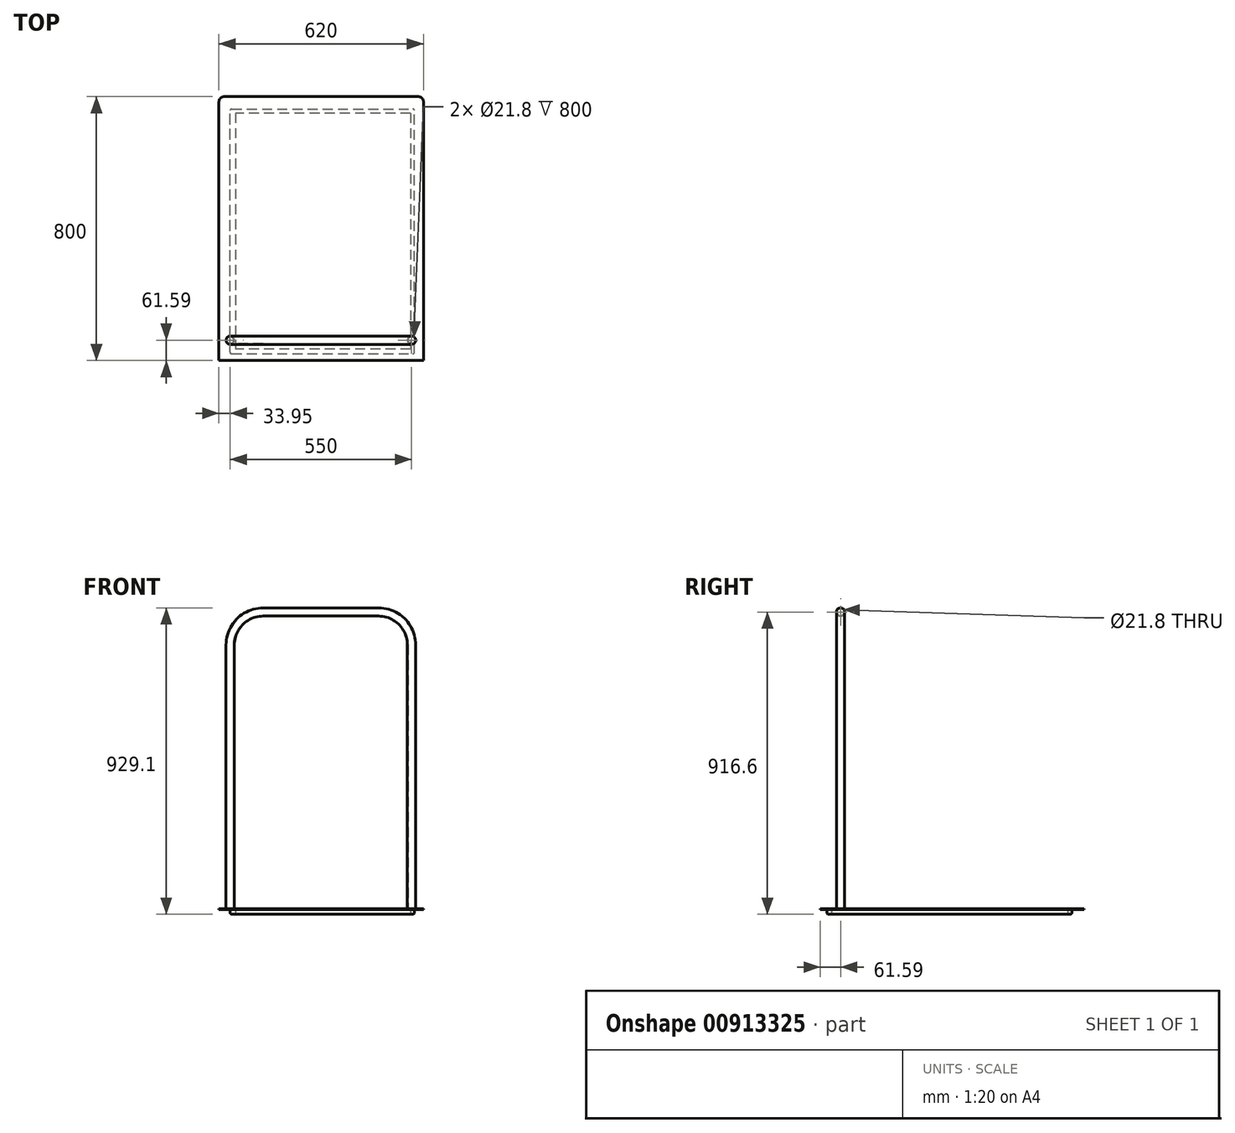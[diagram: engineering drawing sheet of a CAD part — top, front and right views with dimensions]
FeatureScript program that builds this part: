
annotation { "Feature Type Name" : "Feature", "Feature Type Description" : "" }
export const myFeature = defineFeature(function(context is Context, id is Id, definition is map)
    precondition{}
    {
        {
            var Q0;
            Q0=qCreatedBy(makeId("Top.planeOp"),FACE);
            var sketch = newSketch(context, id + "F0", { "sketchPlane" : qUnion([Q0])});
            skCircle(sketch, "E0", {"center": v(0, 0) * mm, "radius": 12.5 * mm});
            skCircle(sketch, "E1", {"center": v(0, 0) * mm, "radius": 10.9 * mm});
            skSolve(sketch);
        }
        {
            var Q0;
            Q0=qCreatedBy(makeId("Front.planeOp"),FACE);
            var sketch = newSketch(context, id + "F1", { "sketchPlane" : qUnion([Q0])});
            skLineSegment(sketch, "E2.top", {"start": v(100, 900) * mm, "end": v(450, 900) * mm});
            skLineSegment(sketch, "E2.left", {"start": v(0, 0) * mm, "end": v(0, 800) * mm});
            skLineSegment(sketch, "E2.right", {"start": v(550, 0) * mm, "end": v(550, 800) * mm});
            skPoint(sketch, "E3.visualSharp", {"position": v(550, 900) * mm});
            skArc(sketch, "E3.filletArc", {"start": v(550, 800) * mm, "mid": v(520.71, 870.71) * mm, "end": v(450, 900) * mm});
            skPoint(sketch, "E4.visualSharp", {"position": v(0, 900) * mm});
            skArc(sketch, "E4.filletArc", {"start": v(100, 900) * mm, "mid": v(29.29, 870.71) * mm, "end": v(0, 800) * mm});
            skSolve(sketch);
        }
        {
            var Q0;
            Q0=makeQuery(id+"F0.imprint","IMPRINT",FACE,{"disambiguationData":[TD([[makeQuery(id+"F0.imprint","IMPRINT",EDGE,{"derivedFrom":sQuery(id+"F0.wireOp",EDGE,"E0")}),1.0]])]});
            var Q1;
            Q1=sQuery(id+"F1.wireOp",EDGE,"E2.left");
            var Q2;
            Q2=sQuery(id+"F1.wireOp",EDGE,"E4.filletArc");
            var Q3;
            Q3=sQuery(id+"F1.wireOp",EDGE,"E2.top");
            var Q4;
            Q4=sQuery(id+"F1.wireOp",EDGE,"E3.filletArc");
            var Q5;
            Q5=sQuery(id+"F1.wireOp",EDGE,"E2.right");
            sweep(context, id + "F2", {"profiles" : qUnion([Q0]), "path" : qUnion([Q1, Q2, Q3, Q4, Q5])});
        }
        {
            var Q0;
            Q0=qCreatedBy(makeId("Top.planeOp"),FACE);
            var sketch = newSketch(context, id + "F3", { "sketchPlane" : qUnion([Q0])});
            skLineSegment(sketch, "E5.bottom", {"start": v(-33.95, 738.4) * mm, "end": v(586.05, 738.4) * mm});
            skLineSegment(sketch, "E5.top", {"start": v(-33.95, -61.6) * mm, "end": v(586.05, -61.6) * mm});
            skLineSegment(sketch, "E5.left", {"start": v(-33.95, 738.4) * mm, "end": v(-33.95, -61.6) * mm});
            skLineSegment(sketch, "E5.right", {"start": v(586.05, 738.4) * mm, "end": v(586.05, -61.6) * mm});
            skSolve(sketch);
        }
        {
            var Q0;
            Q0 = qSketchRegion(id + "F3", true);
            extrude(context, id + "F4", {"entities" : qUnion([Q0]), "operationType" : NewBodyOperationType.ADD, "oppositeDirection" : true, "depth" : 1.6 * mm, "offsetDistance" : 25 * mm});
        }
        {
            var Q0;
            Q0=makeQuery(id+"F4.opExtrude","SWEPT_EDGE",EDGE,{"disambiguationData":[OSD([sQuery(id+"F3.wireOp",EDGE,"E5.bottom"),sQuery(id+"F3.wireOp",EDGE,"E5.left")])]});
            fillet(context, id + "F5", {"entities" : qUnion([Q0]), "radius" : 15 * mm, "tangentPropagation" : true, "allowEdgeOverflow" : false});
        }
        {
            var Q0;
            Q0=makeQuery(id+"F4.opExtrude","SWEPT_EDGE",EDGE,{"disambiguationData":[OSD([sQuery(id+"F3.wireOp",EDGE,"E5.bottom"),sQuery(id+"F3.wireOp",EDGE,"E5.right")])]});
            fillet(context, id + "F6", {"entities" : qUnion([Q0]), "radius" : 15 * mm, "tangentPropagation" : true, "allowEdgeOverflow" : false});
        }
        {
            var Q0;
            Q0=makeQuery(id+"F4.opExtrude","CAP_FACE",FACE,{"disambiguationData":[OSD([sQuery(id+"F3.wireOp",EDGE,"E5.bottom"),sQuery(id+"F3.wireOp",EDGE,"E5.top"),sQuery(id+"F3.wireOp",EDGE,"E5.left"),sQuery(id+"F3.wireOp",EDGE,"E5.right")])],"isStart":false});
            var sketch = newSketch(context, id + "F7", { "sketchPlane" : qUnion([Q0])});
            skLineSegment(sketch, "E6.bottom", {"start": v(0, 41.36) * mm, "end": v(558.6, 41.36) * mm});
            skLineSegment(sketch, "E6.top", {"start": v(0, -701.3) * mm, "end": v(558.6, -701.3) * mm});
            skLineSegment(sketch, "E6.left", {"start": v(0, 41.36) * mm, "end": v(0, -701.3) * mm});
            skLineSegment(sketch, "E6.right", {"start": v(558.6, 41.36) * mm, "end": v(558.6, -701.3) * mm});
            skSolve(sketch);
        }
        {
            var Q0;
            Q0 = qSketchRegion(id + "F7", true);
            extrude(context, id + "F8", {"entities" : qUnion([Q0]), "operationType" : NewBodyOperationType.ADD, "depth" : 15 * mm, "offsetDistance" : 25 * mm});
        }
        {
            var Q0;
            Q0=makeQuery(id+"F8.opExtrude","CAP_FACE",FACE,{"disambiguationData":[OSD([sQuery(id+"F7.wireOp",EDGE,"E6.bottom"),sQuery(id+"F7.wireOp",EDGE,"E6.top"),sQuery(id+"F7.wireOp",EDGE,"E6.left"),sQuery(id+"F7.wireOp",EDGE,"E6.right")])],"isStart":false});
            var sketch = newSketch(context, id + "F9", { "sketchPlane" : qUnion([Q0])});
            skLineSegment(sketch, "E7.bottom", {"start": v(547, -688.5) * mm, "end": v(16.5, -688.5) * mm});
            skLineSegment(sketch, "E7.top", {"start": v(547, 26.83) * mm, "end": v(16.5, 26.83) * mm});
            skLineSegment(sketch, "E7.left", {"start": v(547, -688.5) * mm, "end": v(547, 26.83) * mm});
            skLineSegment(sketch, "E7.right", {"start": v(16.5, -688.5) * mm, "end": v(16.5, 26.83) * mm});
            skSolve(sketch);
        }
        {
            var Q0;
            Q0 = qSketchRegion(id + "F9", true);
            extrude(context, id + "F10", {"entities" : qUnion([Q0]), "operationType" : NewBodyOperationType.REMOVE, "oppositeDirection" : true, "depth" : 15 * mm, "offsetDistance" : 25 * mm});
        }
        {
            var Q0;
            Q0=makeQuery(id+"F8.opExtrude","CAP_EDGE",EDGE,{"disambiguationData":[OSD([sQuery(id+"F7.wireOp",EDGE,"E6.right")])],"isStart":false});
            var Q1;
            Q1=makeQuery(id+"F10.boolean.opBoolean","COPY",EDGE,{"derivedFrom":makeQuery(id+"F10.opExtrude","CAP_EDGE",EDGE,{"disambiguationData":[OSD([sQuery(id+"F9.wireOp",EDGE,"E7.left")])],"isStart":true})});
            var Q2;
            Q2=makeQuery(id+"F8.opExtrude","CAP_EDGE",EDGE,{"disambiguationData":[OSD([sQuery(id+"F7.wireOp",EDGE,"E6.bottom")])],"isStart":false});
            var Q3;
            Q3=makeQuery(id+"F10.boolean.opBoolean","COPY",EDGE,{"derivedFrom":makeQuery(id+"F10.opExtrude","CAP_EDGE",EDGE,{"disambiguationData":[OSD([sQuery(id+"F9.wireOp",EDGE,"E7.top")])],"isStart":true})});
            var Q4;
            Q4=makeQuery(id+"F10.boolean.opBoolean","COPY",EDGE,{"derivedFrom":makeQuery(id+"F10.opExtrude","CAP_EDGE",EDGE,{"disambiguationData":[OSD([sQuery(id+"F9.wireOp",EDGE,"E7.right")])],"isStart":true})});
            var Q5;
            Q5=makeQuery(id+"F8.opExtrude","CAP_EDGE",EDGE,{"disambiguationData":[OSD([sQuery(id+"F7.wireOp",EDGE,"E6.left")])],"isStart":false});
            var Q6;
            Q6=makeQuery(id+"F10.boolean.opBoolean","COPY",EDGE,{"derivedFrom":makeQuery(id+"F10.opExtrude","CAP_EDGE",EDGE,{"disambiguationData":[OSD([sQuery(id+"F9.wireOp",EDGE,"E7.bottom")])],"isStart":true})});
            var Q7;
            Q7=makeQuery(id+"F8.opExtrude","CAP_EDGE",EDGE,{"disambiguationData":[OSD([sQuery(id+"F7.wireOp",EDGE,"E6.top")])],"isStart":false});
            var Q8;
            Q8=makeQuery(id+"F8.opExtrude","SWEPT_EDGE",EDGE,{"disambiguationData":[OSD([sQuery(id+"F7.wireOp",EDGE,"E6.top"),sQuery(id+"F7.wireOp",EDGE,"E6.right")])]});
            var Q9;
            Q9=makeQuery(id+"F8.opExtrude","SWEPT_EDGE",EDGE,{"disambiguationData":[OSD([sQuery(id+"F7.wireOp",EDGE,"E6.top"),sQuery(id+"F7.wireOp",EDGE,"E6.left")])]});
            var Q10;
            Q10=makeQuery(id+"F8.opExtrude","SWEPT_EDGE",EDGE,{"disambiguationData":[OSD([sQuery(id+"F7.wireOp",EDGE,"E6.bottom"),sQuery(id+"F7.wireOp",EDGE,"E6.left")])]});
            fillet(context, id + "F11", {"entities" : qUnion([Q0, Q1, Q2, Q3, Q4, Q5, Q6, Q7, Q8, Q9, Q10]), "radius" : 5 * mm, "tangentPropagation" : true, "allowEdgeOverflow" : false});
        }
        {
            var Q0;
            Q0=makeQuery(id+"F11.opFillet","BLEND_EDGE",EDGE,{"blendedFrom":[makeQuery(id+"F8.opExtrude","CAP_EDGE",EDGE,{"disambiguationData":[OSD([sQuery(id+"F7.wireOp",EDGE,"E6.bottom")])],"isStart":false}),makeQuery(id+"F8.opExtrude","CAP_EDGE",EDGE,{"disambiguationData":[OSD([sQuery(id+"F7.wireOp",EDGE,"E6.right")])],"isStart":false})],"blendedInto":[]});
            var Q1;
            Q1=makeQuery(id+"F8.opExtrude","SWEPT_EDGE",EDGE,{"disambiguationData":[OSD([sQuery(id+"F7.wireOp",EDGE,"E6.bottom"),sQuery(id+"F7.wireOp",EDGE,"E6.right")])]});
            fillet(context, id + "F12", {"entities" : qUnion([Q0, Q1]), "radius" : 5 * mm, "tangentPropagation" : true, "allowEdgeOverflow" : false});
        }
    });
